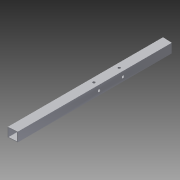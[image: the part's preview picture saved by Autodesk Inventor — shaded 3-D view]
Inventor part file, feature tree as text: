
AUTODESK INVENTOR PART (.ipt)
format: ipt  version: 2013 (Build 170138000, 138)  size: 123,904 bytes
history: native  units: in
note: dims shown in document units (in); Inventor stores cm internally (conversion verified against a paired STEP export)
features: extrude x6, sketch x5
ambient origin geometry x8: Origin, YZ Plane, XZ Plane, XY Plane, X Axis, Y Axis, Z Axis, Center Point
bodies: Solid1 (feature_tree)
feature tree (11):
  extrude  "Extrusion1"  Depth=1.0in
  extrude  "Extrusion2"  Depth=20.0in TaperAngle=0.0deg
  extrude  "Extrusion3"  Depth=0.1321in
  extrude  "Extrusion4"  Depth=1.0in TaperAngle=0.0deg
  extrude  "Extrusion5"  Depth=1.0in TaperAngle=0.0deg
  extrude  "Extrusion6"  Depth=1.0in TaperAngle=0.0deg
  sketch  "Sketch1"  dims[d0=1.0in d2=1.0in]
  sketch  "Sketch3"  dims[d3=0.0625in d4=20.0in d5=0.0in]
  sketch  "Sketch4"  dims[d9=20.0in d10=0.0in d12=0.1321in]
  sketch  "Sketch5"  dims[d13=17.5in d14=1.0in d15=0.0in]
  sketch  "Sketch6"  dims[d16=1.0in d17=0.0in d18=1.0in d19=0.0in d20=1.0in d21=0.0in]
